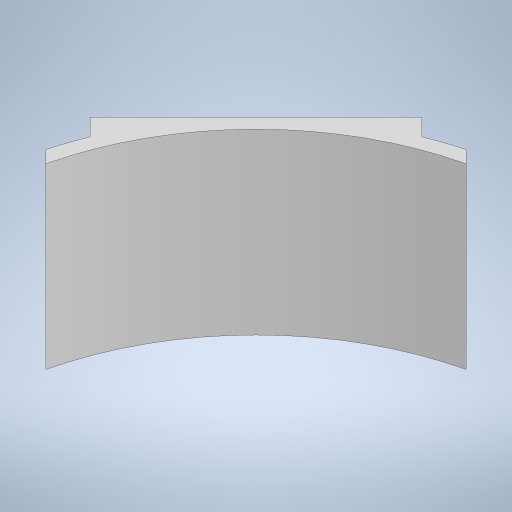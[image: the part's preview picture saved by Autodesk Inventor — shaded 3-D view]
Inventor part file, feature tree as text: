
AUTODESK INVENTOR PART (.ipt)
format: ipt  version: 2023 (Build 270158000, 158)  size: 226,304 bytes
history: native  units: in
note: dims shown in document units (in); Inventor stores cm internally (conversion verified against a paired STEP export)
features: extrude x3, sketch x3
ambient origin geometry x8: Origin, YZ Plane, XZ Plane, XY Plane, X Axis, Y Axis, Z Axis, Center Point
bodies: Solid1 (feature_tree)
feature tree (6):
  extrude  "Extrusion1"  Depth=2.0in
  extrude  "Extrusion2"  Depth=0.79in
  extrude  "Extrusion3"  Depth=0.5in
  sketch  "Sketch1"  dims[d0=1.9in d1=2.0in]
  sketch  "Sketch2"  dims[d2=0.6in d3=0.0in d4=0.79in]
  sketch  "Sketch3"  dims[d5=0.36in d6=0.0in d7=0.5in d8=0.5in d9=0.36in d10=0.0in]
